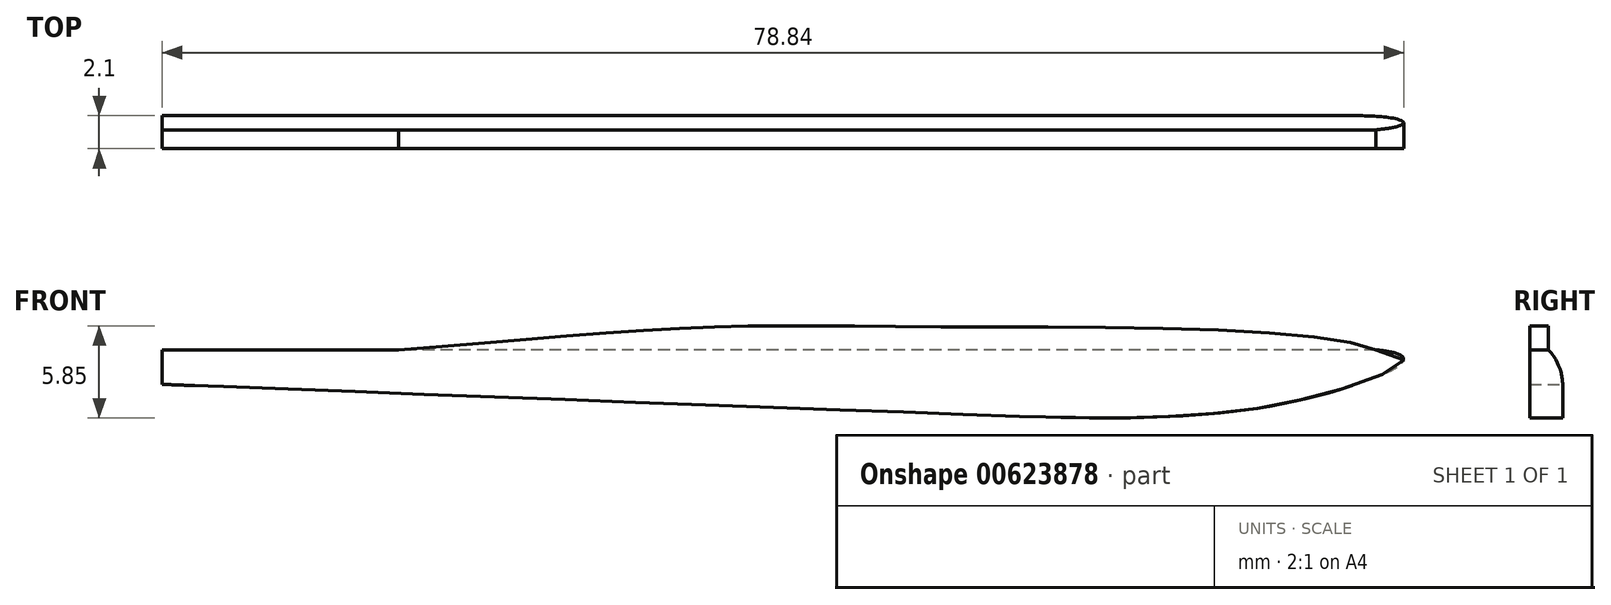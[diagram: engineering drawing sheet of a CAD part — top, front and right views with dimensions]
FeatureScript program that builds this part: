
annotation { "Feature Type Name" : "Feature", "Feature Type Description" : "" }
export const myFeature = defineFeature(function(context is Context, id is Id, definition is map)
    precondition{}
    {
        {
            var Q0;
            Q0=qCreatedBy(makeId("Front.planeOp"),FACE);
            var sketch = newSketch(context, id + "F0", { "sketchPlane" : qUnion([Q0])});
            skFitSpline(sketch, "E0", {"points": [v(0, 0) * mm, v(50.51, -1.9) * mm, v(75.82, 0) * mm, v(77.08, 2.19) * mm], "startDerivative": vector(86.95, -3.32) * mm, "endDerivative": vector(-90.34, 8.22) * mm});
            skFitSpline(sketch, "E1", {"points": [v(77.08, 2.19) * mm, v(50.03, 3.65) * mm, v(33.54, 3.6) * mm, v(15, 2.19) * mm], "startDerivative": vector(-28.6, 12.44) * mm, "endDerivative": vector(-64.17, -4.73) * mm});
            skLineSegment(sketch, "E2", {"start": v(15, 2.19) * mm, "end": v(0, 2.19) * mm});
            skLineSegment(sketch, "E3", {"start": v(0, 0) * mm, "end": v(0, 2.19) * mm});
            skSolve(sketch);
        }
        {
            var Q0;
            Q0 = qSketchRegion(id + "F0", true);
            extrude(context, id + "F1", {"entities" : qUnion([Q0]), "depth" : 2.1 * mm, "offsetDistance" : 25 * mm});
        }
        {
            var Q0;
            Q0=qCreatedBy(makeId("Front.planeOp"),FACE);
            var sketch = newSketch(context, id + "F2", { "sketchPlane" : qUnion([Q0])});
            skLineSegment(sketch, "E4", {"start": v(14.82, 2.17) * mm, "end": v(79.46, 1.55) * mm});
            skLineSegment(sketch, "E5", {"start": v(79.46, 1.55) * mm, "end": v(79.46, 4.25) * mm});
            skLineSegment(sketch, "E6", {"start": v(79.46, 4.25) * mm, "end": v(14.82, 4.25) * mm});
            skLineSegment(sketch, "E7", {"start": v(14.82, 4.25) * mm, "end": v(14.82, 2.17) * mm});
            skSolve(sketch);
        }
        {
            var Q0;
            Q0 = qSketchRegion(id + "F2", true);
            extrude(context, id + "F3", {"entities" : qUnion([Q0]), "operationType" : NewBodyOperationType.REMOVE, "depth" : 0.9 * mm, "offsetDistance" : 25 * mm});
        }
        {
            var Q0;
            Q0=makeQuery(id+"F3.boolean.opBoolean","COPY",EDGE,{"derivedFrom":makeQuery(id+"F3.opExtrude","CAP_EDGE",EDGE,{"disambiguationData":[OSD([sQuery(id+"F2.wireOp",EDGE,"E4")])],"isStart":false})});
            fillet(context, id + "F4", {"entities" : qUnion([Q0]), "radius" : 5 * mm, "tangentPropagation" : true, "allowEdgeOverflow" : false});
        }
        {
            var Q0;
            Q0=makeQuery(id+"F4.opFillet","BLEND_EDGE",EDGE,{"blendedFrom":[makeQuery(id+"F3.boolean.opBoolean","COPY",EDGE,{"derivedFrom":makeQuery(id+"F3.opExtrude","CAP_EDGE",EDGE,{"disambiguationData":[OSD([sQuery(id+"F2.wireOp",EDGE,"E4")])],"isStart":false})}),makeQuery(id+"F1.opExtrude","CAP_FACE",FACE,{"disambiguationData":[OSD([sQuery(id+"F0.wireOp",EDGE,"E0"),sQuery(id+"F0.wireOp",EDGE,"E1"),sQuery(id+"F0.wireOp",EDGE,"E2"),sQuery(id+"F0.wireOp",EDGE,"E3")])],"isStart":true})],"blendedInto":[makeQuery(id+"F1.opExtrude","CAP_FACE",FACE,{"disambiguationData":[OSD([sQuery(id+"F0.wireOp",EDGE,"E0"),sQuery(id+"F0.wireOp",EDGE,"E1"),sQuery(id+"F0.wireOp",EDGE,"E2"),sQuery(id+"F0.wireOp",EDGE,"E3")])],"isStart":true})]});
            fillet(context, id + "F5", {"entities" : qUnion([Q0]), "radius" : 3.3 * mm, "tangentPropagation" : true, "allowEdgeOverflow" : false});
        }
    });
